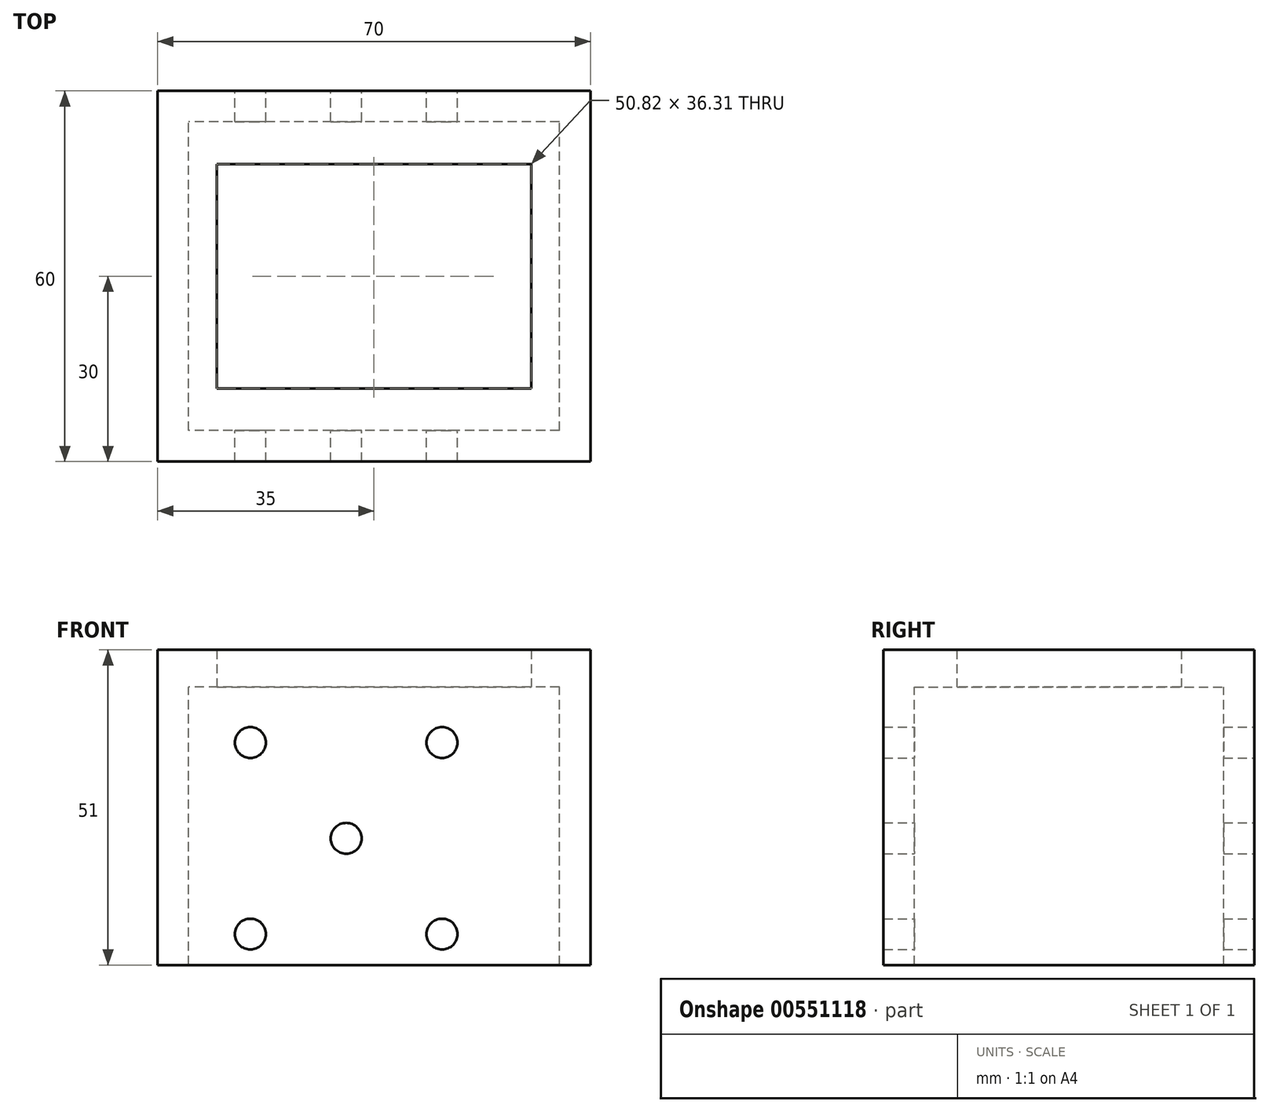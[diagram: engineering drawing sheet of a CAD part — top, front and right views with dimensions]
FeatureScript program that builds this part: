
annotation { "Feature Type Name" : "Feature", "Feature Type Description" : "" }
export const myFeature = defineFeature(function(context is Context, id is Id, definition is map)
    precondition{}
    {
        {
            var Q0;
            Q0=qCreatedBy(makeId("Top.planeOp"),FACE);
            var sketch = newSketch(context, id + "F0", { "sketchPlane" : qUnion([Q0])});
            skLineSegment(sketch, "E0.bottom", {"start": v(35, 30) * mm, "end": v(-35, 30) * mm});
            skLineSegment(sketch, "E0.top", {"start": v(35, -30) * mm, "end": v(-35, -30) * mm});
            skLineSegment(sketch, "E0.left", {"start": v(35, 30) * mm, "end": v(35, -30) * mm});
            skLineSegment(sketch, "E0.right", {"start": v(-35, 30) * mm, "end": v(-35, -30) * mm});
            skPoint(sketch, "E0.middle", {"position": v(0, 0) * mm});
            skLineSegment(sketch, "E1.bottom", {"start": v(-25.41, 18.15) * mm, "end": v(25.41, 18.15) * mm});
            skLineSegment(sketch, "E1.top", {"start": v(-25.41, -18.15) * mm, "end": v(25.41, -18.15) * mm});
            skLineSegment(sketch, "E1.left", {"start": v(-25.41, 18.15) * mm, "end": v(-25.41, -18.15) * mm});
            skLineSegment(sketch, "E1.right", {"start": v(25.41, 18.15) * mm, "end": v(25.41, -18.15) * mm});
            skSolve(sketch);
        }
        {
            var Q0;
            Q0=makeQuery(id+"F0.imprint","IMPRINT",FACE,{"disambiguationData":[TD([[makeQuery(id+"F0.imprint","IMPRINT",EDGE,{"derivedFrom":sQuery(id+"F0.wireOp",EDGE,"E0.bottom")}),1.0]])]});
            extrude(context, id + "F1", {"entities" : qUnion([Q0]), "depth" : 6 * mm, "offsetDistance" : 25 * mm});
        }
        {
            var Q0;
            Q0=makeQuery(id+"F1.opExtrude","CAP_FACE",FACE,{"disambiguationData":[OSD([sQuery(id+"F0.wireOp",EDGE,"E0.bottom"),sQuery(id+"F0.wireOp",EDGE,"E0.top"),sQuery(id+"F0.wireOp",EDGE,"E0.left"),sQuery(id+"F0.wireOp",EDGE,"E0.right")])],"isStart":true});
            var sketch = newSketch(context, id + "F2", { "sketchPlane" : qUnion([Q0])});
            skLineSegment(sketch, "E2.bottom", {"start": v(35, 30) * mm, "end": v(-35, 30) * mm});
            skLineSegment(sketch, "E2.top", {"start": v(35, -30) * mm, "end": v(-35, -30) * mm});
            skLineSegment(sketch, "E2.left", {"start": v(35, 30) * mm, "end": v(35, -30) * mm});
            skLineSegment(sketch, "E2.right", {"start": v(-35, 30) * mm, "end": v(-35, -30) * mm});
            skPoint(sketch, "E2.middle", {"position": v(0, 0) * mm});
            skLineSegment(sketch, "E3.bottom", {"start": v(30, 25) * mm, "end": v(-30, 25) * mm});
            skLineSegment(sketch, "E3.top", {"start": v(30, -25) * mm, "end": v(-30, -25) * mm});
            skLineSegment(sketch, "E3.left", {"start": v(30, 25) * mm, "end": v(30, -25) * mm});
            skLineSegment(sketch, "E3.right", {"start": v(-30, 25) * mm, "end": v(-30, -25) * mm});
            skSolve(sketch);
        }
        {
            var Q0;
            Q0=makeQuery(id+"F2.imprint","IMPRINT",FACE,{"disambiguationData":[TD([[makeQuery(id+"F2.imprint","IMPRINT",EDGE,{"derivedFrom":sQuery(id+"F2.wireOp",EDGE,"E2.bottom")}),1.0]])]});
            extrude(context, id + "F3", {"entities" : qUnion([Q0]), "operationType" : NewBodyOperationType.ADD, "depth" : 45 * mm, "offsetDistance" : 25 * mm});
        }
        {
            var Q0;
            Q0=makeQuery(id+"F3.boolean.opBoolean","MERGE",FACE,{"derivedFrom":[makeQuery(id+"F1.opExtrude","SWEPT_FACE",FACE,{"disambiguationData":[OSD([sQuery(id+"F0.wireOp",EDGE,"E0.bottom")])]}),makeQuery(id+"F3.opExtrude","SWEPT_FACE",FACE,{"disambiguationData":[OSD([sQuery(id+"F2.wireOp",EDGE,"E2.top")])]})]});
            var sketch = newSketch(context, id + "F4", { "sketchPlane" : qUnion([Q0])});
            skCircle(sketch, "E4", {"center": v(20, -40) * mm, "radius": 2 * mm});
            skCircle(sketch, "E5.0.1.0", {"center": v(20, -9) * mm, "radius": 2 * mm});
            skCircle(sketch, "E5.1.0.0", {"center": v(-11, -40) * mm, "radius": 2 * mm});
            skCircle(sketch, "E5.1.1.0", {"center": v(-11, -9) * mm, "radius": 2 * mm});
            skLineSegment(sketch, "E5.direction1", {"start": v(20, -40) * mm, "end": v(-11, -40) * mm, "construction": true});
            skLineSegment(sketch, "E5.direction2", {"start": v(20, -40) * mm, "end": v(20, -9) * mm, "construction": true});
            skCircle(sketch, "E6", {"center": v(4.5, -24.5) * mm, "radius": 3.5 * mm});
            skSolve(sketch);
        }
        {
            var Q0;
            Q0=sQuery(id+"F4.wireOp",VERTEX,"E4.center");
            var Q1;
            Q1=sQuery(id+"F4.wireOp",VERTEX,"E5.1.0.0.center");
            var Q2;
            Q2=sQuery(id+"F4.wireOp",VERTEX,"E6.center");
            var Q3;
            Q3=sQuery(id+"F4.wireOp",VERTEX,"E5.0.1.0.center");
            var Q4;
            Q4=sQuery(id+"F4.wireOp",VERTEX,"E5.1.1.0.center");
            var Q5;
            Q5=makeQuery(id+"F1.opExtrude","SWEPT_BODY",BODY,{"disambiguationData":[OSD([sQuery(id+"F0.wireOp",EDGE,"E0.bottom"),sQuery(id+"F0.wireOp",EDGE,"E0.top"),sQuery(id+"F0.wireOp",EDGE,"E0.left"),sQuery(id+"F0.wireOp",EDGE,"E0.right"),sQuery(id+"F0.wireOp",EDGE,"E1.bottom"),sQuery(id+"F0.wireOp",EDGE,"E1.top"),sQuery(id+"F0.wireOp",EDGE,"E1.left"),sQuery(id+"F0.wireOp",EDGE,"E1.right")])]});
            hole(context, id + "F5", {"style" : HoleStyle.SIMPLE, "endStyle" : HoleEndStyle.THROUGH, "holeDiameter" : 5 * mm, "isTappedThrough" : true, "tappedDepth" : 12 * mm, "tapClearance" : 3, "locations" : qUnion([Q0, Q1, Q2, Q3, Q4]), "scope" : qUnion([Q5])});
        }
    });
